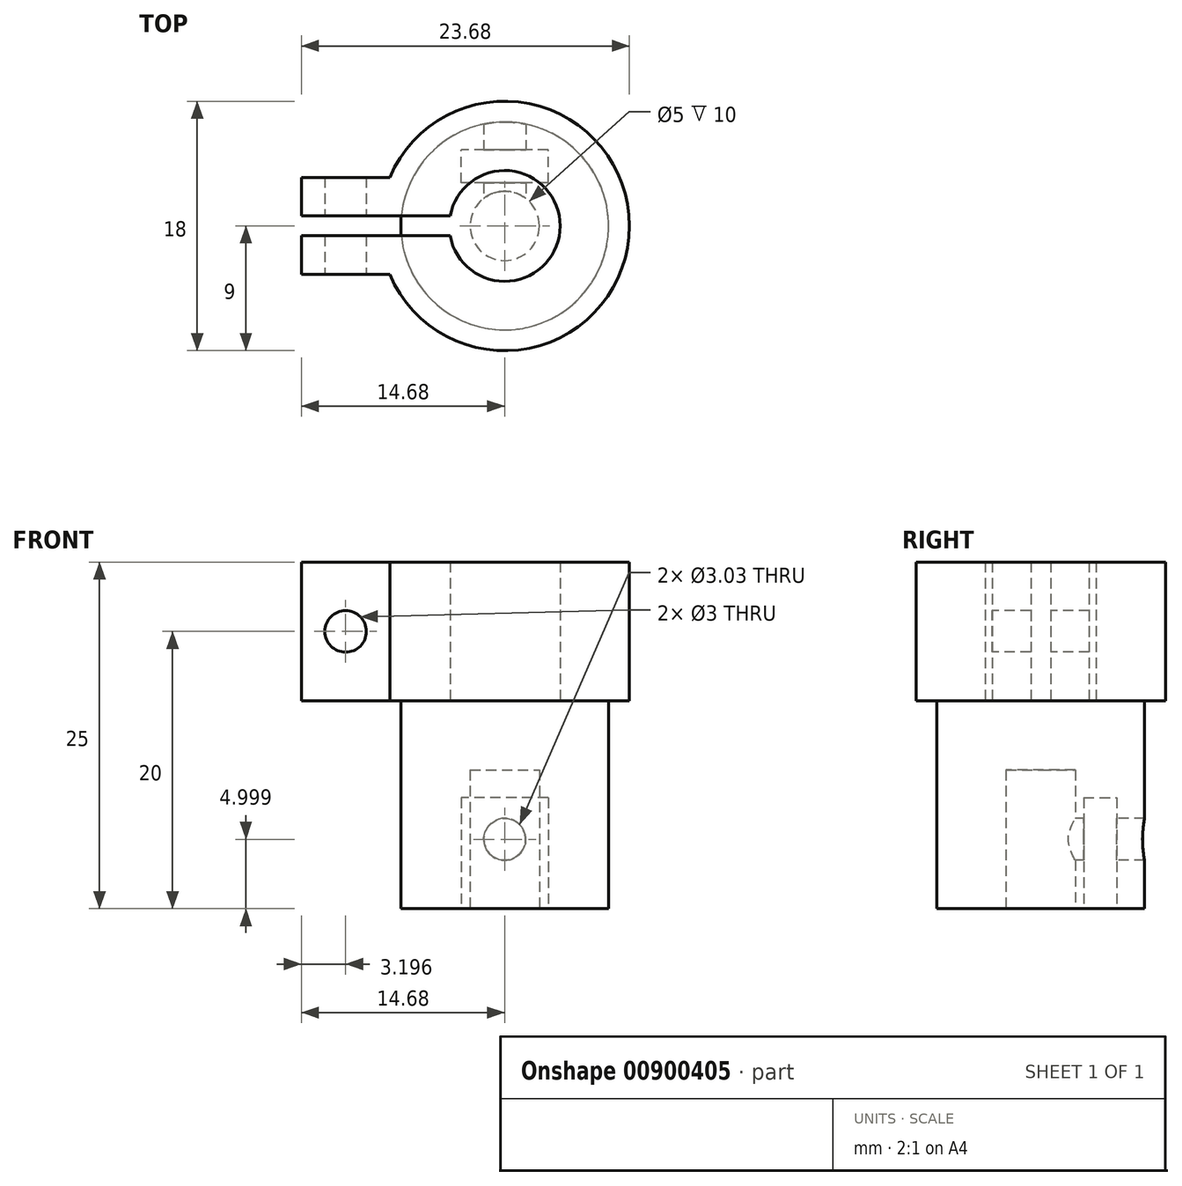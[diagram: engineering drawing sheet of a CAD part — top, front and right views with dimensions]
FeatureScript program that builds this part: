
annotation { "Feature Type Name" : "Feature", "Feature Type Description" : "" }
export const myFeature = defineFeature(function(context is Context, id is Id, definition is map)
    precondition{}
    {
        {
            var Q0;
            Q0=qCreatedBy(makeId("Top.planeOp"),FACE);
            var sketch = newSketch(context, id + "F0", { "sketchPlane" : qUnion([Q0])});
            skArc(sketch, "E0", {"start": v(-8.3, -3.5) * mm, "mid": v(9, 0) * mm, "end": v(-8.3, 3.5) * mm});
            skArc(sketch, "E1", {"start": v(-3.94, -0.71) * mm, "mid": v(4, 0) * mm, "end": v(-3.94, 0.71) * mm});
            skLineSegment(sketch, "E2.bottom", {"start": v(-14.68, -3.5) * mm, "end": v(-8.3, -3.5) * mm});
            skLineSegment(sketch, "E2.top", {"start": v(-14.68, 3.5) * mm, "end": v(-8.3, 3.5) * mm});
            skLineSegment(sketch, "E2.left", {"start": v(-14.68, -3.5) * mm, "end": v(-14.68, -0.71) * mm});
            skPoint(sketch, "E2.right.start.orphan", {"position": v(14.68, -3.5) * mm});
            skPoint(sketch, "E3.orphan", {"position": v(14.68, 3.5) * mm});
            skLineSegment(sketch, "E4.bottom", {"start": v(-14.68, -0.71) * mm, "end": v(-3.94, -0.71) * mm});
            skLineSegment(sketch, "E4.top", {"start": v(-14.68, 0.71) * mm, "end": v(-3.94, 0.71) * mm});
            skPoint(sketch, "E4.left.start.orphan", {"position": v(-14.54, -0.71) * mm});
            skPoint(sketch, "E5.orphan", {"position": v(-14.54, 0.71) * mm});
            skLineSegment(sketch, "E6.trimOffspring", {"start": v(-14.68, 0.71) * mm, "end": v(-14.68, 3.5) * mm});
            skPoint(sketch, "E4.right.end.orphan", {"position": v(14.54, 0.71) * mm});
            skPoint(sketch, "E4.right.start.orphan", {"position": v(14.54, -0.71) * mm});
            skSolve(sketch);
        }
        {
            var Q0;
            Q0=makeQuery(id+"F0.imprint","IMPRINT",FACE,{"disambiguationData":[TD([[makeQuery(id+"F0.imprint","IMPRINT",EDGE,{"derivedFrom":sQuery(id+"F0.wireOp",EDGE,"E0")}),1.0]])]});
            extrude(context, id + "F1", {"entities" : qUnion([Q0]), "depth" : 10 * mm, "offsetDistance" : 25 * mm});
        }
        {
            var Q0;
            Q0=makeQuery(id+"F1.opExtrude","CAP_FACE",FACE,{"disambiguationData":[OSD([sQuery(id+"F0.wireOp",EDGE,"E0"),sQuery(id+"F0.wireOp",EDGE,"E1"),sQuery(id+"F0.wireOp",EDGE,"E2.bottom"),sQuery(id+"F0.wireOp",EDGE,"E2.top"),sQuery(id+"F0.wireOp",EDGE,"E2.left"),sQuery(id+"F0.wireOp",EDGE,"E4.bottom"),sQuery(id+"F0.wireOp",EDGE,"E4.top"),sQuery(id+"F0.wireOp",EDGE,"E6.trimOffspring")])],"isStart":true});
            var sketch = newSketch(context, id + "F2", { "sketchPlane" : qUnion([Q0])});
            skCircle(sketch, "E7", {"center": v(0, 0) * mm, "radius": 7.5 * mm});
            skSolve(sketch);
        }
        {
            var Q0;
            Q0 = qSketchRegion(id + "F2", true);
            extrude(context, id + "F3", {"entities" : qUnion([Q0]), "operationType" : NewBodyOperationType.ADD, "depth" : 15 * mm, "offsetDistance" : 25 * mm});
        }
        {
            var Q0;
            Q0=makeQuery(id+"F3.opExtrude","CAP_FACE",FACE,{"disambiguationData":[OSD([sQuery(id+"F2.wireOp",EDGE,"E7")])],"isStart":false});
            var sketch = newSketch(context, id + "F4", { "sketchPlane" : qUnion([Q0])});
            skCircle(sketch, "E8", {"center": v(0, 0) * mm, "radius": 2.5 * mm});
            skSolve(sketch);
        }
        {
            var Q0;
            Q0=makeQuery(id+"F4.imprint","IMPRINT",FACE,{"disambiguationData":[TD([[makeQuery(id+"F4.imprint","IMPRINT",EDGE,{"derivedFrom":sQuery(id+"F4.wireOp",EDGE,"E8")}),1.0]])]});
            extrude(context, id + "F5", {"entities" : qUnion([Q0]), "operationType" : NewBodyOperationType.REMOVE, "oppositeDirection" : true, "depth" : 10 * mm, "offsetDistance" : 25 * mm});
        }
        {
            var Q0;
            Q0=makeQuery(id+"F1.opExtrude","SWEPT_FACE",FACE,{"disambiguationData":[OSD([sQuery(id+"F0.wireOp",EDGE,"E2.bottom")])]});
            var sketch = newSketch(context, id + "F6", { "sketchPlane" : qUnion([Q0])});
            skCircle(sketch, "E9", {"center": v(-11.48, 5) * mm, "radius": 1.5 * mm});
            skPoint(sketch, "E9.centerSnap0", {"position": v(-11.48, 0) * mm});
            skPoint(sketch, "E9.centerSnap1", {"position": v(-14.68, 5) * mm});
            skSolve(sketch);
        }
        {
            var Q0;
            Q0=makeQuery(id+"F6.imprint","IMPRINT",FACE,{"disambiguationData":[TD([[makeQuery(id+"F6.imprint","IMPRINT",EDGE,{"derivedFrom":sQuery(id+"F6.wireOp",EDGE,"E9")}),1.0]])]});
            extrude(context, id + "F7", {"entities" : qUnion([Q0]), "operationType" : NewBodyOperationType.REMOVE, "oppositeDirection" : true, "depth" : 25 * mm, "offsetDistance" : 25 * mm});
        }
        {
            var Q0;
            Q0=qCreatedBy(makeId("Front.planeOp"),FACE);
            var sketch = newSketch(context, id + "F8", { "sketchPlane" : qUnion([Q0])});
            skCircle(sketch, "E10", {"center": v(0, -10) * mm, "radius": 1.51 * mm});
            skSolve(sketch);
        }
        {
            var Q0;
            Q0=makeQuery(id+"F8.imprint","IMPRINT",FACE,{"disambiguationData":[TD([[makeQuery(id+"F8.imprint","IMPRINT",EDGE,{"derivedFrom":sQuery(id+"F8.wireOp",EDGE,"E10")}),1.0]])]});
            extrude(context, id + "F9", {"entities" : qUnion([Q0]), "operationType" : NewBodyOperationType.REMOVE, "oppositeDirection" : true, "depth" : 25 * mm, "offsetDistance" : 25 * mm});
        }
        {
            var Q0;
            Q0=makeQuery(id+"F3.opExtrude","CAP_FACE",FACE,{"disambiguationData":[OSD([sQuery(id+"F2.wireOp",EDGE,"E7")])],"isStart":false});
            var sketch = newSketch(context, id + "F10", { "sketchPlane" : qUnion([Q0])});
            skLineSegment(sketch, "E11.bottom", {"start": v(3.15, -3.1) * mm, "end": v(-3.15, -3.1) * mm});
            skLineSegment(sketch, "E11.top", {"start": v(3.15, -5.5) * mm, "end": v(-3.15, -5.5) * mm});
            skLineSegment(sketch, "E11.left", {"start": v(3.15, -3.1) * mm, "end": v(3.15, -5.5) * mm});
            skLineSegment(sketch, "E11.right", {"start": v(-3.15, -3.1) * mm, "end": v(-3.15, -5.5) * mm});
            skPoint(sketch, "E11.middle", {"position": v(0, -4.3) * mm});
            skSolve(sketch);
        }
        {
            var Q0;
            Q0=makeQuery(id+"F10.imprint","IMPRINT",FACE,{"disambiguationData":[TD([[makeQuery(id+"F10.imprint","IMPRINT",EDGE,{"derivedFrom":sQuery(id+"F10.wireOp",EDGE,"E11.bottom")}),1.0]])]});
            extrude(context, id + "F11", {"entities" : qUnion([Q0]), "operationType" : NewBodyOperationType.REMOVE, "oppositeDirection" : true, "depth" : 8 * mm, "offsetDistance" : 25 * mm});
        }
    });
